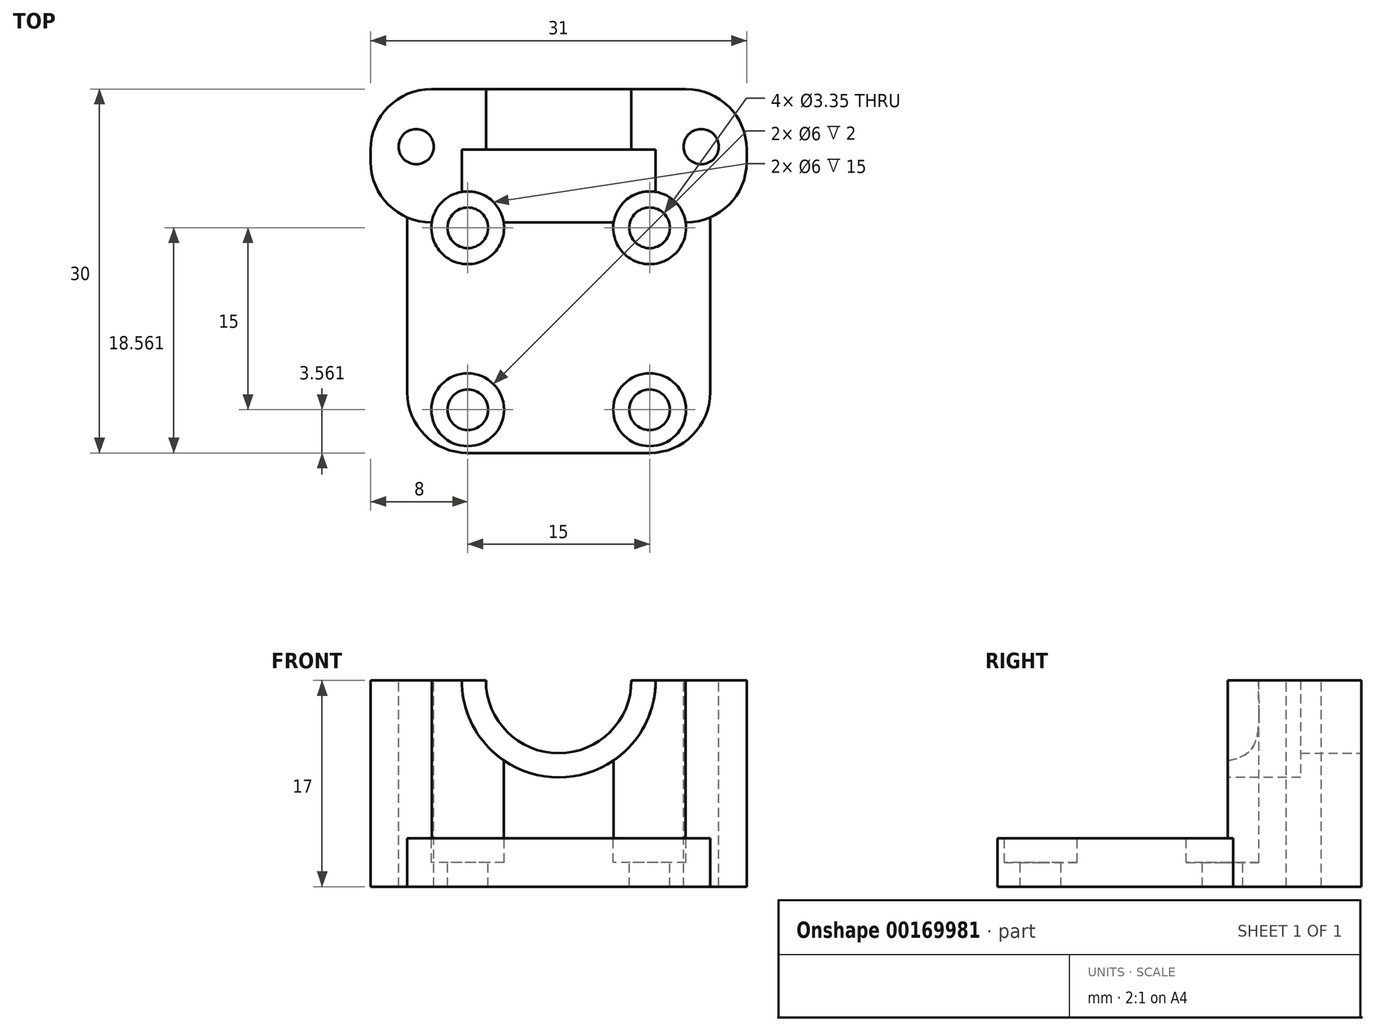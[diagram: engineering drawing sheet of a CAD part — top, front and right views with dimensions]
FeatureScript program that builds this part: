
annotation { "Feature Type Name" : "Feature", "Feature Type Description" : "" }
export const myFeature = defineFeature(function(context is Context, id is Id, definition is map)
    precondition{}
    {
        {
            var Q0;
            Q0=qCreatedBy(makeId("Top.planeOp"),FACE);
            var sketch = newSketch(context, id + "F0", { "sketchPlane" : qUnion([Q0])});
            skLineSegment(sketch, "E0.bottom", {"start": v(0, 0) * mm, "end": v(25, 0) * mm});
            skLineSegment(sketch, "E0.top", {"start": v(0, 30) * mm, "end": v(25, 30) * mm});
            skLineSegment(sketch, "E0.left", {"start": v(0, 0) * mm, "end": v(0, 30) * mm});
            skLineSegment(sketch, "E0.right", {"start": v(25, 0) * mm, "end": v(25, 30) * mm});
            skSolve(sketch);
        }
        {
            var Q0;
            Q0=qSketchRegion(id+"F0",true);
            extrude(context, id + "F1", {"entities" : qUnion([Q0]), "depth" : 4 * mm});
        }
        {
            var Q0;
            Q0=makeQuery(id+"F1.opExtrude","CAP_FACE",FACE,{"disambiguationData":[OSD([sQuery(id+"F0.wireOp",EDGE,"E0.bottom"),sQuery(id+"F0.wireOp",EDGE,"E0.top"),sQuery(id+"F0.wireOp",EDGE,"E0.left"),sQuery(id+"F0.wireOp",EDGE,"E0.right")])],"isStart":false});
            var sketch = newSketch(context, id + "F2", { "sketchPlane" : qUnion([Q0])});
            skCircle(sketch, "E1", {"center": v(5, 18.56) * mm, "radius": 1.68 * mm});
            skCircle(sketch, "E2", {"center": v(20, 18.56) * mm, "radius": 1.68 * mm});
            skCircle(sketch, "E3", {"center": v(5, 3.56) * mm, "radius": 1.68 * mm});
            skCircle(sketch, "E4", {"center": v(20, 3.56) * mm, "radius": 1.68 * mm});
            skLineSegment(sketch, "E5", {"start": v(5, 18.56) * mm, "end": v(0, 18.56) * mm});
            skLineSegment(sketch, "E6", {"start": v(20, 3.56) * mm, "end": v(25, 3.56) * mm});
            skCircle(sketch, "E7", {"center": v(5, 18.56) * mm, "radius": 3 * mm});
            skCircle(sketch, "E8", {"center": v(20, 18.56) * mm, "radius": 3 * mm});
            skCircle(sketch, "E9", {"center": v(5, 3.56) * mm, "radius": 3 * mm});
            skCircle(sketch, "E10", {"center": v(20, 3.56) * mm, "radius": 3 * mm});
            skSolve(sketch);
        }
        {
            var Q0;
            Q0=makeQuery(id+"F2.imprint","IMPRINT",FACE,{"disambiguationData":[TD([[makeQuery(id+"F2.imprint","IMPRINT",EDGE,{"derivedFrom":sQuery(id+"F2.wireOp",EDGE,"E1")}),1.0]])]});
            var Q1;
            Q1=makeQuery(id+"F2.imprint","IMPRINT",FACE,{"disambiguationData":[TD([[makeQuery(id+"F2.imprint","IMPRINT",EDGE,{"derivedFrom":sQuery(id+"F2.wireOp",EDGE,"E2")}),1.0]])]});
            var Q2;
            Q2=makeQuery(id+"F2.imprint","IMPRINT",FACE,{"disambiguationData":[TD([[makeQuery(id+"F2.imprint","IMPRINT",EDGE,{"derivedFrom":sQuery(id+"F2.wireOp",EDGE,"E4")}),1.0]])]});
            var Q3;
            Q3=makeQuery(id+"F2.imprint","IMPRINT",FACE,{"disambiguationData":[TD([[makeQuery(id+"F2.imprint","IMPRINT",EDGE,{"derivedFrom":sQuery(id+"F2.wireOp",EDGE,"E3")}),1.0]])]});
            extrude(context, id + "F3", {"entities" : qUnion([Q0, Q1, Q2, Q3]), "operationType" : NewBodyOperationType.REMOVE, "oppositeDirection" : true, "depth" : 25 * mm});
        }
        {
            var Q0;
            Q0=makeQuery(id+"F1.opExtrude","CAP_FACE",FACE,{"disambiguationData":[OSD([sQuery(id+"F0.wireOp",EDGE,"E0.bottom"),sQuery(id+"F0.wireOp",EDGE,"E0.top"),sQuery(id+"F0.wireOp",EDGE,"E0.left"),sQuery(id+"F0.wireOp",EDGE,"E0.right")])],"isStart":false});
            var sketch = newSketch(context, id + "F4", { "sketchPlane" : qUnion([Q0])});
            skLineSegment(sketch, "E11.bottom", {"start": v(0, 30) * mm, "end": v(25, 30) * mm});
            skLineSegment(sketch, "E11.top", {"start": v(0, 19) * mm, "end": v(25, 19) * mm});
            skLineSegment(sketch, "E11.left", {"start": v(0, 30) * mm, "end": v(0, 19) * mm});
            skLineSegment(sketch, "E11.right", {"start": v(25, 30) * mm, "end": v(25, 19) * mm});
            skSolve(sketch);
        }
        {
            var Q0;
            Q0=qSketchRegion(id+"F4",true);
            extrude(context, id + "F5", {"entities" : qUnion([Q0]), "operationType" : NewBodyOperationType.ADD, "depth" : 13 * mm});
        }
        {
            var Q0;
            Q0=makeQuery(id+"F5.boolean.opBoolean","MERGE",FACE,{"derivedFrom":[makeQuery(id+"F1.opExtrude","SWEPT_FACE",FACE,{"disambiguationData":[OSD([sQuery(id+"F0.wireOp",EDGE,"E0.top")])]}),makeQuery(id+"F5.opExtrude","SWEPT_FACE",FACE,{"disambiguationData":[OSD([sQuery(id+"F4.wireOp",EDGE,"E11.bottom")])]})]});
            var sketch = newSketch(context, id + "F6", { "sketchPlane" : qUnion([Q0])});
            skCircle(sketch, "E12", {"center": v(-12.5, 17) * mm, "radius": 6 * mm});
            skSolve(sketch);
        }
        {
            var Q0;
            {var subQ0=makeQuery(id+"F5.opExtrude","CAP_EDGE",EDGE,{"disambiguationData":[OSD([sQuery(id+"F4.wireOp",EDGE,"E11.bottom")])],"isStart":false});var subQ1=sQuery(id+"F6.wireOp",EDGE,"E12");var subQ3=makeQuery(id+"F6.imprint","INTERSECT",VERTEX,{"disambiguationData":[OD(0.0)],"derivedFrom":[subQ0,subQ1]});Q0=makeQuery(id+"F6.imprint","IMPRINT",FACE,{"disambiguationData":[TD([[makeQuery(id+"F6.imprint","IMPRINT",EDGE,{"disambiguationData":[TD([[subQ3,1.0]])],"derivedFrom":subQ1}),1.0]])]});}
            extrude(context, id + "F7", {"entities" : qUnion([Q0]), "operationType" : NewBodyOperationType.REMOVE, "oppositeDirection" : true, "depth" : 6 * mm});
        }
        {
            var Q0;
            Q0=makeQuery(id+"F5.opExtrude","SWEPT_FACE",FACE,{"disambiguationData":[OSD([sQuery(id+"F4.wireOp",EDGE,"E11.top")])]});
            var sketch = newSketch(context, id + "F8", { "sketchPlane" : qUnion([Q0])});
            skCircle(sketch, "E13", {"center": v(12.5, 17) * mm, "radius": 8 * mm});
            skSolve(sketch);
        }
        {
            var Q0;
            Q0=qSketchRegion(id+"F8",true);
            extrude(context, id + "F9", {"entities" : qUnion([Q0]), "operationType" : NewBodyOperationType.REMOVE, "oppositeDirection" : true, "depth" : 6 * mm});
        }
        {
            var Q0;
            Q0=makeQuery(id+"F2.imprint","IMPRINT",FACE,{"disambiguationData":[TD([[makeQuery(id+"F2.imprint","IMPRINT",EDGE,{"derivedFrom":sQuery(id+"F2.wireOp",EDGE,"E1")}),-1.0]])]});
            var Q1;
            Q1=makeQuery(id+"F2.imprint","IMPRINT",FACE,{"disambiguationData":[TD([[makeQuery(id+"F2.imprint","IMPRINT",EDGE,{"derivedFrom":sQuery(id+"F2.wireOp",EDGE,"E2")}),-1.0]])]});
            var Q2;
            Q2=makeQuery(id+"F2.imprint","IMPRINT",FACE,{"disambiguationData":[TD([[makeQuery(id+"F2.imprint","IMPRINT",EDGE,{"derivedFrom":sQuery(id+"F2.wireOp",EDGE,"E4")}),-1.0]])]});
            var Q3;
            Q3=makeQuery(id+"F2.imprint","IMPRINT",FACE,{"disambiguationData":[TD([[makeQuery(id+"F2.imprint","IMPRINT",EDGE,{"derivedFrom":sQuery(id+"F2.wireOp",EDGE,"E3")}),-1.0]])]});
            extrude(context, id + "F10", {"entities" : qUnion([Q0, Q1, Q2, Q3]), "operationType" : NewBodyOperationType.REMOVE, "oppositeDirection" : true, "depth" : 2 * mm});
        }
        {
            var Q0;
            Q0=makeQuery(id+"F5.boolean.opBoolean","MERGE",FACE,{"derivedFrom":[makeQuery(id+"F1.opExtrude","SWEPT_FACE",FACE,{"disambiguationData":[OSD([sQuery(id+"F0.wireOp",EDGE,"E0.left")])]}),makeQuery(id+"F5.opExtrude","SWEPT_FACE",FACE,{"disambiguationData":[OSD([sQuery(id+"F4.wireOp",EDGE,"E11.left")])]})]});
            var sketch = newSketch(context, id + "F11", { "sketchPlane" : qUnion([Q0])});
            skLineSegment(sketch, "E14.bottom", {"start": v(-30, 0) * mm, "end": v(-19, 0) * mm});
            skLineSegment(sketch, "E14.top", {"start": v(-30, 17) * mm, "end": v(-19, 17) * mm});
            skLineSegment(sketch, "E14.left", {"start": v(-30, 0) * mm, "end": v(-30, 17) * mm});
            skLineSegment(sketch, "E14.right", {"start": v(-19, 0) * mm, "end": v(-19, 17) * mm});
            skSolve(sketch);
        }
        {
            var Q0;
            Q0=qSketchRegion(id+"F11",true);
            extrude(context, id + "F12", {"entities" : qUnion([Q0]), "operationType" : NewBodyOperationType.ADD, "depth" : 3 * mm});
        }
        {
            var Q0;
            Q0=makeQuery(id+"F1.opExtrude","SWEPT_EDGE",EDGE,{"disambiguationData":[OSD([sQuery(id+"F0.wireOp",EDGE,"E0.bottom"),sQuery(id+"F0.wireOp",EDGE,"E0.left")])]});
            var Q1;
            Q1=makeQuery(id+"F1.opExtrude","SWEPT_EDGE",EDGE,{"disambiguationData":[OSD([sQuery(id+"F0.wireOp",EDGE,"E0.bottom"),sQuery(id+"F0.wireOp",EDGE,"E0.right")])]});
            fillet(context, id + "F13", {"entities" : qUnion([Q0, Q1]), "radius" : 5 * mm, "tangentPropagation" : true, "allowEdgeOverflow" : false});
        }
        {
            var Q0;
            Q0=makeQuery(id+"F5.boolean.opBoolean","MERGE",FACE,{"derivedFrom":[makeQuery(id+"F1.opExtrude","SWEPT_FACE",FACE,{"disambiguationData":[OSD([sQuery(id+"F0.wireOp",EDGE,"E0.right")])]}),makeQuery(id+"F5.opExtrude","SWEPT_FACE",FACE,{"disambiguationData":[OSD([sQuery(id+"F4.wireOp",EDGE,"E11.right")])]})]});
            var sketch = newSketch(context, id + "F14", { "sketchPlane" : qUnion([Q0])});
            skLineSegment(sketch, "E15.bottom", {"start": v(30, 0) * mm, "end": v(19, 0) * mm});
            skLineSegment(sketch, "E15.top", {"start": v(30, 17) * mm, "end": v(19, 17) * mm});
            skLineSegment(sketch, "E15.left", {"start": v(30, 0) * mm, "end": v(30, 17) * mm});
            skLineSegment(sketch, "E15.right", {"start": v(19, 0) * mm, "end": v(19, 17) * mm});
            skSolve(sketch);
        }
        {
            var Q0;
            Q0=qSketchRegion(id+"F14",true);
            extrude(context, id + "F15", {"entities" : qUnion([Q0]), "operationType" : NewBodyOperationType.ADD, "depth" : 3 * mm});
        }
        {
            var Q0;
            {var subQ0=sQuery(id+"F4.wireOp",EDGE,"E11.bottom");var subQ1=sQuery(id+"F4.wireOp",EDGE,"E11.top");var subQ2=sQuery(id+"F4.wireOp",EDGE,"E11.left");Q0=makeQuery(id+"F9.boolean.opBoolean","SPLIT",FACE,{"disambiguationData":[TD([makeQuery(id+"F1.opExtrude","SWEPT_FACE",FACE,{"disambiguationData":[OSD([sQuery(id+"F0.wireOp",EDGE,"E0.left")])]})])],"derivedFrom":makeQuery(id+"F5.opExtrude","CAP_FACE",FACE,{"disambiguationData":[OSD([subQ0,subQ1,subQ2,sQuery(id+"F4.wireOp",EDGE,"E11.right")])],"isStart":false})});}
            var sketch = newSketch(context, id + "F16", { "sketchPlane" : qUnion([Q0])});
            skCircle(sketch, "E16", {"center": v(0.75, 25.25) * mm, "radius": 1.45 * mm});
            skCircle(sketch, "E17", {"center": v(24.25, 25.25) * mm, "radius": 1.45 * mm});
            skSolve(sketch);
        }
        {
            var Q0;
            Q0=qSketchRegion(id+"F16",true);
            extrude(context, id + "F17", {"entities" : qUnion([Q0]), "operationType" : NewBodyOperationType.REMOVE, "oppositeDirection" : true, "depth" : 25 * mm});
        }
        {
            var Q0;
            Q0=makeQuery(id+"F12.opExtrude","CAP_EDGE",EDGE,{"disambiguationData":[OSD([sQuery(id+"F11.wireOp",EDGE,"E14.right")])],"isStart":false});
            var Q1;
            Q1=makeQuery(id+"F15.opExtrude","CAP_EDGE",EDGE,{"disambiguationData":[OSD([sQuery(id+"F14.wireOp",EDGE,"E15.right")])],"isStart":false});
            var Q2;
            Q2=makeQuery(id+"F15.opExtrude","CAP_EDGE",EDGE,{"disambiguationData":[OSD([sQuery(id+"F14.wireOp",EDGE,"E15.left")])],"isStart":false});
            var Q3;
            Q3=makeQuery(id+"F12.opExtrude","CAP_EDGE",EDGE,{"disambiguationData":[OSD([sQuery(id+"F11.wireOp",EDGE,"E14.left")])],"isStart":false});
            fillet(context, id + "F18", {"entities" : qUnion([Q0, Q1, Q2, Q3]), "radius" : 5 * mm, "tangentPropagation" : true, "allowEdgeOverflow" : false});
        }
        {
            var Q0;
            Q0=makeQuery(id+"F2.imprint","IMPRINT",FACE,{"disambiguationData":[TD([[makeQuery(id+"F2.imprint","IMPRINT",EDGE,{"derivedFrom":sQuery(id+"F2.wireOp",EDGE,"E1")}),-1.0]])]});
            var Q1;
            Q1=makeQuery(id+"F2.imprint","IMPRINT",FACE,{"disambiguationData":[TD([[makeQuery(id+"F2.imprint","IMPRINT",EDGE,{"derivedFrom":sQuery(id+"F2.wireOp",EDGE,"E2")}),-1.0]])]});
            var Q2;
            Q2=makeQuery(id+"F2.imprint","IMPRINT",FACE,{"disambiguationData":[TD([[makeQuery(id+"F2.imprint","IMPRINT",EDGE,{"derivedFrom":sQuery(id+"F2.wireOp",EDGE,"E1")}),1.0]])]});
            var Q3;
            Q3=makeQuery(id+"F2.imprint","IMPRINT",FACE,{"disambiguationData":[TD([[makeQuery(id+"F2.imprint","IMPRINT",EDGE,{"derivedFrom":sQuery(id+"F2.wireOp",EDGE,"E2")}),1.0]])]});
            extrude(context, id + "F19", {"entities" : qUnion([Q0, Q1, Q2, Q3]), "operationType" : NewBodyOperationType.REMOVE, "depth" : 25 * mm});
        }
    });
